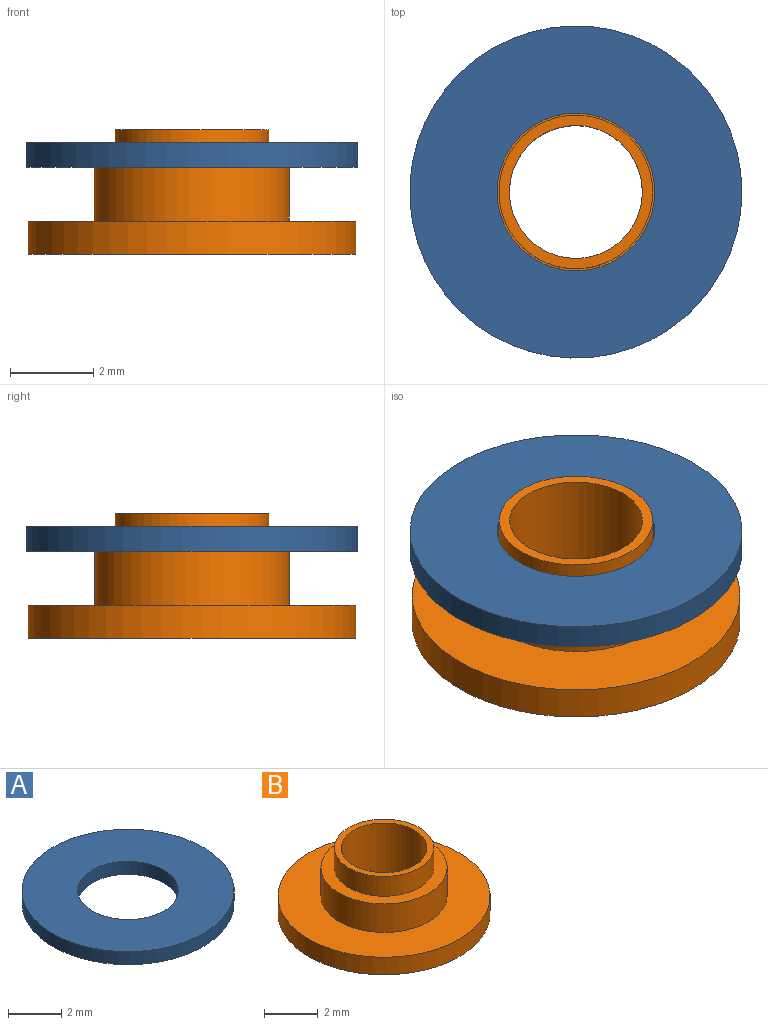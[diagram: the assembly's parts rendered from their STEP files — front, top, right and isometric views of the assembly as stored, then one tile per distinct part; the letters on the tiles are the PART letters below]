
ASSEMBLY  parts=2 mates=2
PART A: 4 faces, bbox 8x8x0.6 mm
  f0: cylinder r=1.9mm len=3.8mm, axis (0,0,-1), area 7.2mm2, adj f2,f3
  f1: cylinder r=4mm len=8mm, axis (0,0,-1), area 15.1mm2, adj f2,f3
  f2: plane 8x8mm, normal (0,0,1), area 38.9mm2, adj f0,f1
  f3: plane 8x8mm, normal (0,0,-1), area 38.9mm2, adj f0,f1
PART B: 8 faces, bbox 7.9x7.9x3 mm
  f0: cylinder r=3.95mm len=7.9mm, axis (0,0,-1), area 19.9mm2, adj f1,f2
  f1: plane 7.9x7.9mm, normal (0,0,1), area 31.7mm2, adj f0,f3
  f2: plane 7.9x7.9mm, normal (0,0,-1), area 41mm2, adj f0,f5
  f3: cylinder r=2.35mm len=4.7mm, axis (0,0,-1), area 19.2mm2, adj f1,f4
  f4: plane 4.7x4.7mm, normal (0,0,1), area 6.6mm2, adj f3,f6
  f5: cylinder r=1.6mm len=3.2mm, axis (0,0,-1), area 30.2mm2, adj f2,f7
  f6: cylinder r=1.85mm len=3.7mm, axis (0,0,-1), area 10.5mm2, adj f4,f7
  f7: plane 3.7x3.7mm, normal (0,0,1), area 2.7mm2, adj f5,f6
PLACE A t=(-6.52,-2.27,1.55)mm
PLACE B t=(-6.52,-2.27,-0.55)mm
MATE cylindrical B.f6 <-> A.f0  axis (0,0,-1) through (-6.52,-2.27,2)mm
MATE parallel A.f1 <-> B.f0  axis (0,0,-1) through (-6.52,-2.27,1.55)mm
